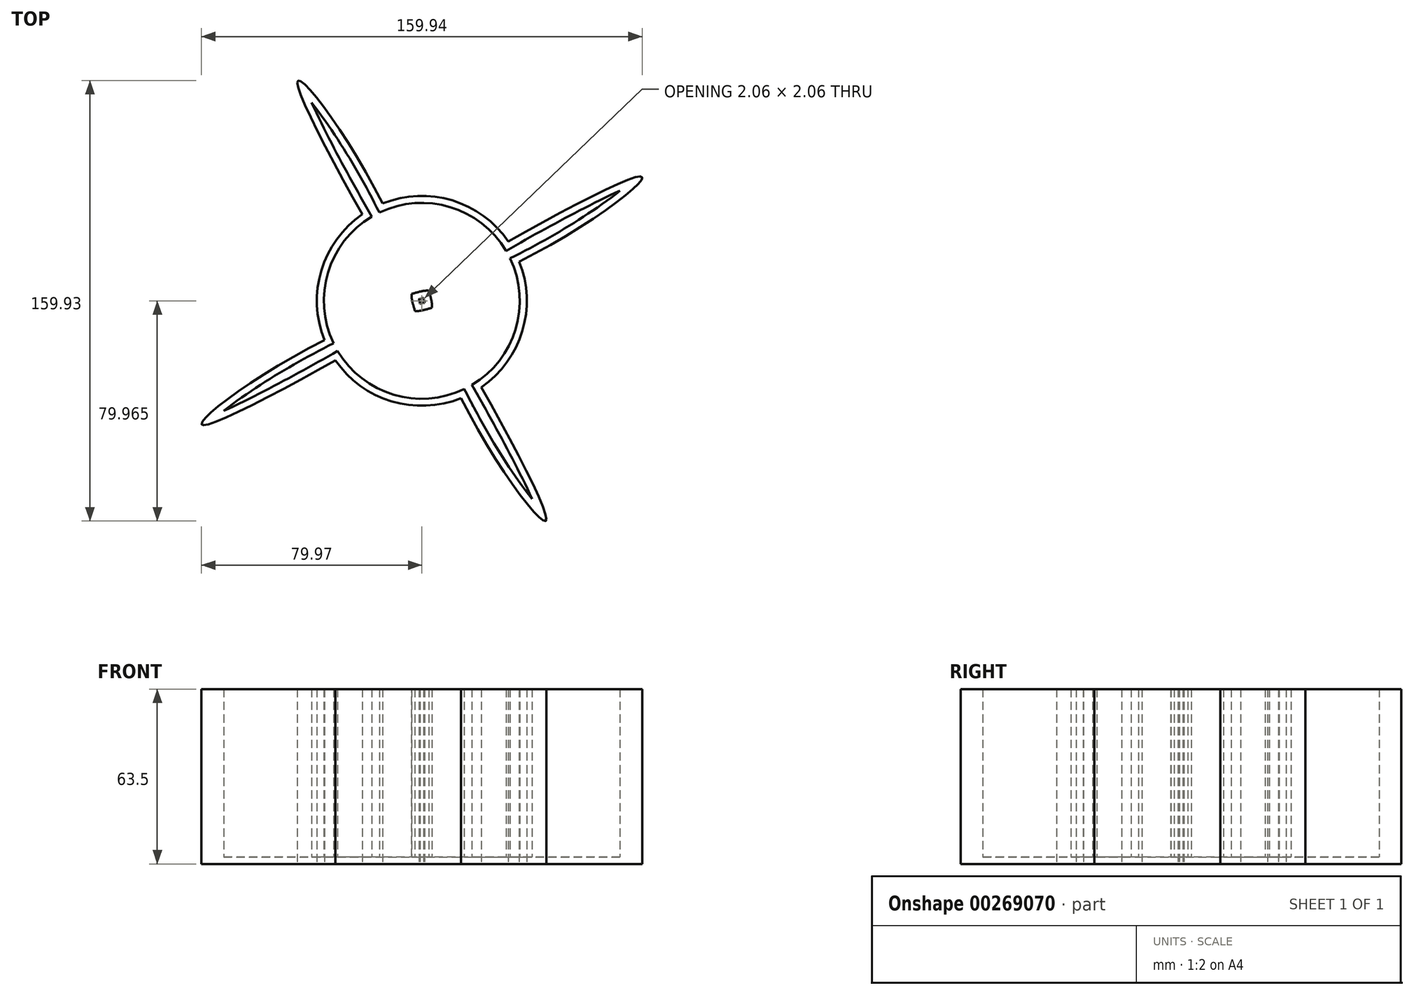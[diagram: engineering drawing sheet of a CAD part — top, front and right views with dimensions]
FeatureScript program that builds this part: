
annotation { "Feature Type Name" : "Feature", "Feature Type Description" : "" }
export const myFeature = defineFeature(function(context is Context, id is Id, definition is map)
    precondition{}
    {
        {
            var Q0;
            Q0=qCreatedBy(makeId("Top.planeOp"),FACE);
            var sketch = newSketch(context, id + "F0", { "sketchPlane" : qUnion([Q0])});
            skCircle(sketch, "E0", {"center": v(0, -2.33) * mm, "radius": 38.1 * mm});
            skSolve(sketch);
        }
        {
            var Q0;
            Q0=makeQuery(id+"F0.imprint","IMPRINT",FACE,{"disambiguationData":[TD([[makeQuery(id+"F0.imprint","IMPRINT",EDGE,{"derivedFrom":sQuery(id+"F0.wireOp",EDGE,"E0")}),1.0]])]});
            var sketch = newSketch(context, id + "F1", { "sketchPlane" : qUnion([Q0])});
            skFitSpline(sketch, "E1", {"points": [v(0, 0) * mm, v(22.4, -52.61) * mm, v(45.1, -80.78) * mm, v(0, 0) * mm]});
            skSolve(sketch);
        }
        {
            var Q0;
            {var subQ0=sQuery(id+"F1.wireOp",EDGE,"E1");var subQ1=makeQuery(id+"F0.imprint","IMPRINT",EDGE,{"derivedFrom":sQuery(id+"F0.wireOp",EDGE,"E0")});var subQ2=makeQuery(id+"F1.imprint","INTERSECT",VERTEX,{"disambiguationData":[OD(0.0)],"derivedFrom":[subQ1,subQ0]});Q0=makeQuery(id+"F1.imprint","IMPRINT",FACE,{"disambiguationData":[TD([[makeQuery(id+"F1.imprint","IMPRINT",EDGE,{"disambiguationData":[TD([[subQ2,1.0]])],"derivedFrom":subQ0}),-1.0]])]});}
            var Q1;
            {var subQ0=sQuery(id+"F1.wireOp",EDGE,"E1");var subQ1=makeQuery(id+"F0.imprint","IMPRINT",EDGE,{"derivedFrom":sQuery(id+"F0.wireOp",EDGE,"E0")});var subQ2=makeQuery(id+"F1.imprint","INTERSECT",VERTEX,{"disambiguationData":[OD(0.0)],"derivedFrom":[subQ1,subQ0]});Q1=makeQuery(id+"F1.imprint","IMPRINT",FACE,{"disambiguationData":[TD([[makeQuery(id+"F1.imprint","IMPRINT",EDGE,{"disambiguationData":[TD([[subQ2,-1.0]])],"derivedFrom":subQ0}),1.0]])]});}
            extrude(context, id + "F2", {"entities" : qUnion([Q0, Q1]), "depth" : 63.5 * mm});
        }
        {
            var Q0;
            {var subQ0=sQuery(id+"F1.wireOp",EDGE,"E1");var subQ1=sQuery(id+"F0.wireOp",EDGE,"E0");var subQ2=makeQuery(id+"F0.imprint","IMPRINT",EDGE,{"derivedFrom":subQ1});var subQ3=makeQuery(id+"F1.imprint","INTERSECT",VERTEX,{"disambiguationData":[OD(0.0)],"derivedFrom":[subQ2,subQ0]});Q0=makeQuery(id+"F2.opExtrude","SWEPT_BODY",BODY,{"disambiguationData":[OSD([subQ1,subQ0]),TDD([makeQuery(id+"F1.imprint","IMPRINT",EDGE,{"disambiguationData":[TD([[subQ3,1.0]])],"derivedFrom":subQ0}),makeQuery(id+"F1.imprint","IMPRINT",EDGE,{"disambiguationData":[TD([[subQ3,1.0]])],"derivedFrom":subQ2})])]});}
            var Q1;
            {var subQ0=sQuery(id+"F1.wireOp",EDGE,"E1");var subQ1=sQuery(id+"F0.wireOp",EDGE,"E0");var subQ2=makeQuery(id+"F0.imprint","IMPRINT",EDGE,{"derivedFrom":subQ1});var subQ3=makeQuery(id+"F1.imprint","INTERSECT",VERTEX,{"disambiguationData":[OD(0.0)],"derivedFrom":[subQ2,subQ0]});Q1=makeQuery(id+"F2.opExtrude","SWEPT_BODY",BODY,{"disambiguationData":[OSD([subQ1,subQ0]),TDD([makeQuery(id+"F1.imprint","IMPRINT",EDGE,{"disambiguationData":[TD([[subQ3,-1.0]])],"derivedFrom":subQ0}),makeQuery(id+"F1.imprint","IMPRINT",EDGE,{"disambiguationData":[TD([[subQ3,-1.0]])],"derivedFrom":subQ2})])]});}
            var Q2;
            Q2=sQuery(id+"F0.wireOp",EDGE,"E0");
            circularPattern(context, id + "F3", {"entities" : qUnion([Q0, Q1]), "axis" : qUnion([Q2]), "angle" : 360 * degree, "instanceCount" : 4, "equalSpace" : true});
        }
        {
            var Q0;
            {var subQ0=sQuery(id+"F1.wireOp",EDGE,"E1");var subQ1=sQuery(id+"F0.wireOp",EDGE,"E0");var subQ2=makeQuery(id+"F0.imprint","IMPRINT",EDGE,{"derivedFrom":subQ1});var subQ3=makeQuery(id+"F1.imprint","INTERSECT",VERTEX,{"disambiguationData":[OD(0.0)],"derivedFrom":[subQ2,subQ0]});Q0=makeQuery(id+"F2.opExtrude","SWEPT_BODY",BODY,{"disambiguationData":[OSD([subQ1,subQ0]),TDD([makeQuery(id+"F1.imprint","IMPRINT",EDGE,{"disambiguationData":[TD([[subQ3,-1.0]])],"derivedFrom":subQ0}),makeQuery(id+"F1.imprint","IMPRINT",EDGE,{"disambiguationData":[TD([[subQ3,-1.0]])],"derivedFrom":subQ2})])]});}
            var Q1;
            {var subQ0=sQuery(id+"F1.wireOp",EDGE,"E1");var subQ1=sQuery(id+"F0.wireOp",EDGE,"E0");var subQ2=makeQuery(id+"F0.imprint","IMPRINT",EDGE,{"derivedFrom":subQ1});var subQ3=makeQuery(id+"F1.imprint","INTERSECT",VERTEX,{"disambiguationData":[OD(0.0)],"derivedFrom":[subQ2,subQ0]});Q1=makeQuery(id+"F3.opPattern","COPY",BODY,{"derivedFrom":makeQuery(id+"F2.opExtrude","SWEPT_BODY",BODY,{"disambiguationData":[OSD([subQ1,subQ0]),TDD([makeQuery(id+"F1.imprint","IMPRINT",EDGE,{"disambiguationData":[TD([[subQ3,1.0]])],"derivedFrom":subQ0}),makeQuery(id+"F1.imprint","IMPRINT",EDGE,{"disambiguationData":[TD([[subQ3,1.0]])],"derivedFrom":subQ2})])]}),"instanceName":"1"});}
            var Q2;
            {var subQ0=sQuery(id+"F1.wireOp",EDGE,"E1");var subQ1=sQuery(id+"F0.wireOp",EDGE,"E0");var subQ2=makeQuery(id+"F0.imprint","IMPRINT",EDGE,{"derivedFrom":subQ1});var subQ3=makeQuery(id+"F1.imprint","INTERSECT",VERTEX,{"disambiguationData":[OD(0.0)],"derivedFrom":[subQ2,subQ0]});Q2=makeQuery(id+"F3.opPattern","COPY",BODY,{"derivedFrom":makeQuery(id+"F2.opExtrude","SWEPT_BODY",BODY,{"disambiguationData":[OSD([subQ1,subQ0]),TDD([makeQuery(id+"F1.imprint","IMPRINT",EDGE,{"disambiguationData":[TD([[subQ3,1.0]])],"derivedFrom":subQ0}),makeQuery(id+"F1.imprint","IMPRINT",EDGE,{"disambiguationData":[TD([[subQ3,1.0]])],"derivedFrom":subQ2})])]}),"instanceName":"3"});}
            var Q3;
            {var subQ0=sQuery(id+"F1.wireOp",EDGE,"E1");var subQ1=sQuery(id+"F0.wireOp",EDGE,"E0");var subQ2=makeQuery(id+"F0.imprint","IMPRINT",EDGE,{"derivedFrom":subQ1});var subQ3=makeQuery(id+"F1.imprint","INTERSECT",VERTEX,{"disambiguationData":[OD(0.0)],"derivedFrom":[subQ2,subQ0]});Q3=makeQuery(id+"F3.opPattern","COPY",BODY,{"derivedFrom":makeQuery(id+"F2.opExtrude","SWEPT_BODY",BODY,{"disambiguationData":[OSD([subQ1,subQ0]),TDD([makeQuery(id+"F1.imprint","IMPRINT",EDGE,{"disambiguationData":[TD([[subQ3,-1.0]])],"derivedFrom":subQ0}),makeQuery(id+"F1.imprint","IMPRINT",EDGE,{"disambiguationData":[TD([[subQ3,-1.0]])],"derivedFrom":subQ2})])]}),"instanceName":"3"});}
            var Q4;
            {var subQ0=sQuery(id+"F1.wireOp",EDGE,"E1");var subQ1=sQuery(id+"F0.wireOp",EDGE,"E0");var subQ2=makeQuery(id+"F0.imprint","IMPRINT",EDGE,{"derivedFrom":subQ1});var subQ3=makeQuery(id+"F1.imprint","INTERSECT",VERTEX,{"disambiguationData":[OD(0.0)],"derivedFrom":[subQ2,subQ0]});Q4=makeQuery(id+"F3.opPattern","COPY",BODY,{"derivedFrom":makeQuery(id+"F2.opExtrude","SWEPT_BODY",BODY,{"disambiguationData":[OSD([subQ1,subQ0]),TDD([makeQuery(id+"F1.imprint","IMPRINT",EDGE,{"disambiguationData":[TD([[subQ3,1.0]])],"derivedFrom":subQ0}),makeQuery(id+"F1.imprint","IMPRINT",EDGE,{"disambiguationData":[TD([[subQ3,1.0]])],"derivedFrom":subQ2})])]}),"instanceName":"2"});}
            var Q5;
            {var subQ0=sQuery(id+"F1.wireOp",EDGE,"E1");var subQ1=sQuery(id+"F0.wireOp",EDGE,"E0");var subQ2=makeQuery(id+"F0.imprint","IMPRINT",EDGE,{"derivedFrom":subQ1});var subQ3=makeQuery(id+"F1.imprint","INTERSECT",VERTEX,{"disambiguationData":[OD(0.0)],"derivedFrom":[subQ2,subQ0]});Q5=makeQuery(id+"F3.opPattern","COPY",BODY,{"derivedFrom":makeQuery(id+"F2.opExtrude","SWEPT_BODY",BODY,{"disambiguationData":[OSD([subQ1,subQ0]),TDD([makeQuery(id+"F1.imprint","IMPRINT",EDGE,{"disambiguationData":[TD([[subQ3,-1.0]])],"derivedFrom":subQ0}),makeQuery(id+"F1.imprint","IMPRINT",EDGE,{"disambiguationData":[TD([[subQ3,-1.0]])],"derivedFrom":subQ2})])]}),"instanceName":"1"});}
            var Q6;
            {var subQ0=sQuery(id+"F1.wireOp",EDGE,"E1");var subQ1=sQuery(id+"F0.wireOp",EDGE,"E0");var subQ2=makeQuery(id+"F0.imprint","IMPRINT",EDGE,{"derivedFrom":subQ1});var subQ3=makeQuery(id+"F1.imprint","INTERSECT",VERTEX,{"disambiguationData":[OD(0.0)],"derivedFrom":[subQ2,subQ0]});Q6=makeQuery(id+"F3.opPattern","COPY",BODY,{"derivedFrom":makeQuery(id+"F2.opExtrude","SWEPT_BODY",BODY,{"disambiguationData":[OSD([subQ1,subQ0]),TDD([makeQuery(id+"F1.imprint","IMPRINT",EDGE,{"disambiguationData":[TD([[subQ3,-1.0]])],"derivedFrom":subQ0}),makeQuery(id+"F1.imprint","IMPRINT",EDGE,{"disambiguationData":[TD([[subQ3,-1.0]])],"derivedFrom":subQ2})])]}),"instanceName":"2"});}
            var Q7;
            {var subQ0=sQuery(id+"F1.wireOp",EDGE,"E1");var subQ1=sQuery(id+"F0.wireOp",EDGE,"E0");var subQ2=makeQuery(id+"F0.imprint","IMPRINT",EDGE,{"derivedFrom":subQ1});var subQ3=makeQuery(id+"F1.imprint","INTERSECT",VERTEX,{"disambiguationData":[OD(0.0)],"derivedFrom":[subQ2,subQ0]});Q7=makeQuery(id+"F2.opExtrude","SWEPT_BODY",BODY,{"disambiguationData":[OSD([subQ1,subQ0]),TDD([makeQuery(id+"F1.imprint","IMPRINT",EDGE,{"disambiguationData":[TD([[subQ3,1.0]])],"derivedFrom":subQ0}),makeQuery(id+"F1.imprint","IMPRINT",EDGE,{"disambiguationData":[TD([[subQ3,1.0]])],"derivedFrom":subQ2})])]});}
            booleanBodies(context, id + "F4", {"operationType" : BooleanOperationType.UNION, "tools" : qUnion([Q0, Q1, Q2, Q3, Q4, Q5, Q6, Q7])});
        }
        {
            var Q0;
            {var subQ0=sQuery(id+"F1.wireOp",EDGE,"E1");var subQ1=sQuery(id+"F0.wireOp",EDGE,"E0");var subQ2=makeQuery(id+"F0.imprint","IMPRINT",EDGE,{"derivedFrom":subQ1});var subQ3=makeQuery(id+"F1.imprint","INTERSECT",VERTEX,{"disambiguationData":[OD(0.0)],"derivedFrom":[subQ2,subQ0]});var subQ5=makeQuery(id+"F2.opExtrude","CAP_FACE",FACE,{"disambiguationData":[OSD([subQ1,subQ0]),TDD([makeQuery(id+"F1.imprint","IMPRINT",EDGE,{"disambiguationData":[TD([[subQ3,1.0]])],"derivedFrom":subQ0}),makeQuery(id+"F1.imprint","IMPRINT",EDGE,{"disambiguationData":[TD([[subQ3,1.0]])],"derivedFrom":subQ2})])],"isStart":false});var subQ6=makeQuery(id+"F2.opExtrude","CAP_FACE",FACE,{"disambiguationData":[OSD([subQ1,subQ0]),TDD([makeQuery(id+"F1.imprint","IMPRINT",EDGE,{"disambiguationData":[TD([[subQ3,-1.0]])],"derivedFrom":subQ0}),makeQuery(id+"F1.imprint","IMPRINT",EDGE,{"disambiguationData":[TD([[subQ3,-1.0]])],"derivedFrom":subQ2})])],"isStart":false});Q0=makeQuery(id+"F4.opBoolean","MERGE",FACE,{"derivedFrom":[subQ6,subQ5,makeQuery(id+"F3.opPattern","COPY",FACE,{"derivedFrom":subQ6,"instanceName":"1"}),makeQuery(id+"F3.opPattern","COPY",FACE,{"derivedFrom":subQ5,"instanceName":"1"}),makeQuery(id+"F3.opPattern","COPY",FACE,{"derivedFrom":subQ6,"instanceName":"2"}),makeQuery(id+"F3.opPattern","COPY",FACE,{"derivedFrom":subQ5,"instanceName":"2"}),makeQuery(id+"F3.opPattern","COPY",FACE,{"derivedFrom":subQ6,"instanceName":"3"}),makeQuery(id+"F3.opPattern","COPY",FACE,{"derivedFrom":subQ5,"instanceName":"3"})]});}
            shell(context, id + "F5", {"entities" : qUnion([Q0]), "thickness" : 2.54 * mm});
        }
    });
